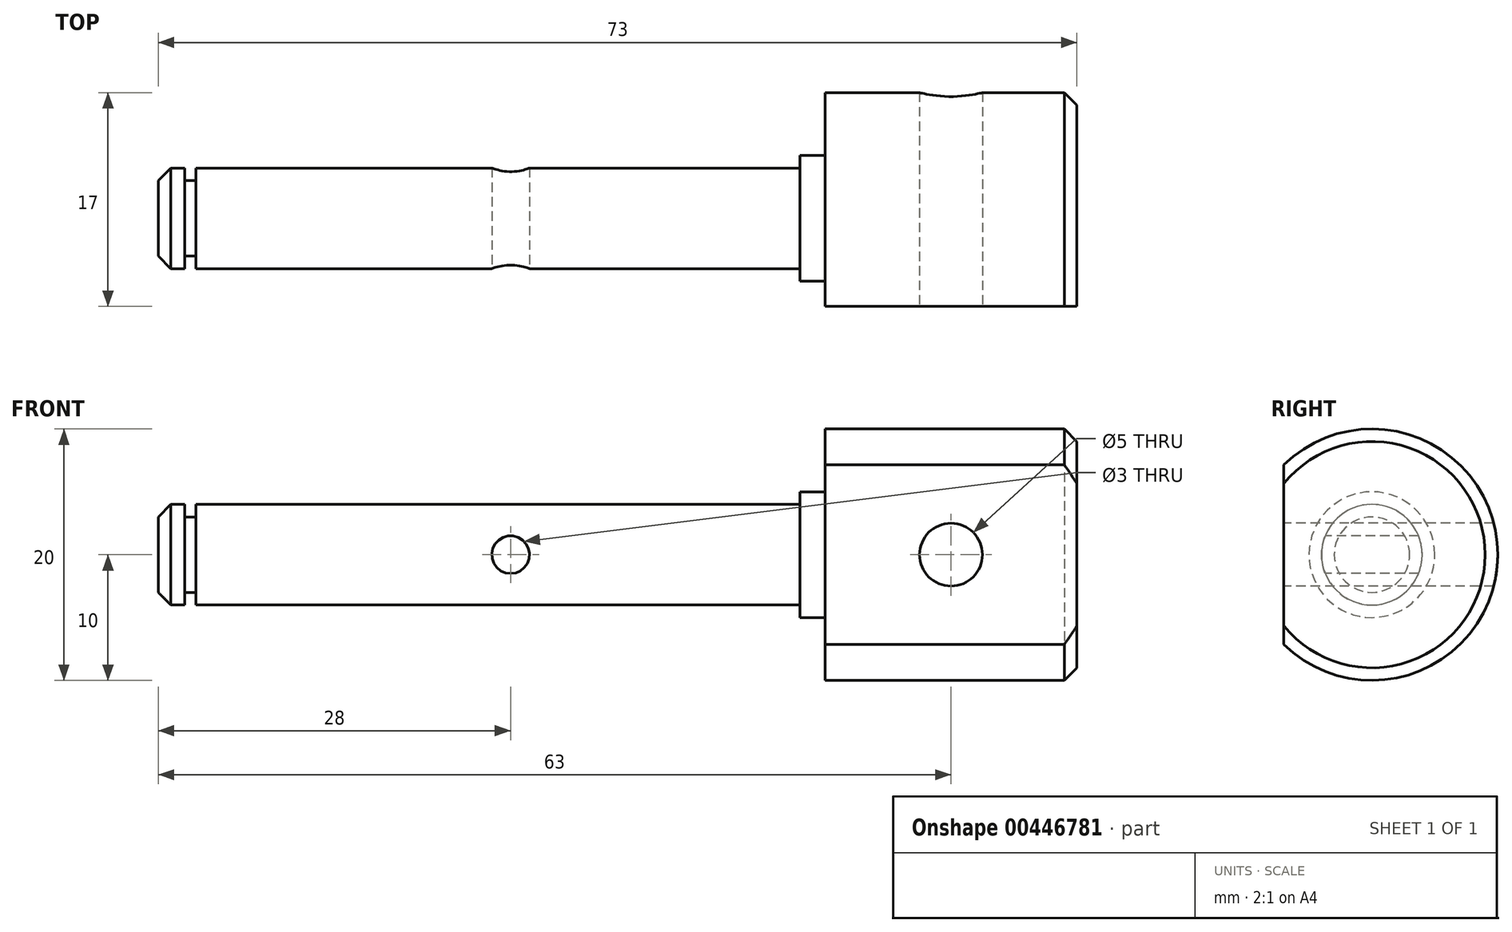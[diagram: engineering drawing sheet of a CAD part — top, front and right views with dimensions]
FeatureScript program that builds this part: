
annotation { "Feature Type Name" : "Feature", "Feature Type Description" : "" }
export const myFeature = defineFeature(function(context is Context, id is Id, definition is map)
    precondition{}
    {
        {
            var Q0;
            Q0=qCreatedBy(makeId("Front.planeOp"),FACE);
            var sketch = newSketch(context, id + "F0", { "sketchPlane" : qUnion([Q0])});
            skLineSegment(sketch, "E0", {"start": v(-56.66, 0) * mm, "end": v(24.86, 0) * mm, "construction": true});
            skLineSegment(sketch, "E1", {"start": v(0, 0) * mm, "end": v(20, 0) * mm});
            skLineSegment(sketch, "E2", {"start": v(20, 0) * mm, "end": v(20, 10) * mm});
            skLineSegment(sketch, "E3", {"start": v(20, 10) * mm, "end": v(0, 10) * mm});
            skLineSegment(sketch, "E4", {"start": v(0, 10) * mm, "end": v(0, 5) * mm});
            skLineSegment(sketch, "E5", {"start": v(0, 5) * mm, "end": v(-2, 5) * mm});
            skLineSegment(sketch, "E6", {"start": v(-2, 5) * mm, "end": v(-2, 4) * mm});
            skLineSegment(sketch, "E7", {"start": v(-2, 4) * mm, "end": v(-50, 4) * mm});
            skLineSegment(sketch, "E8", {"start": v(-50, 4) * mm, "end": v(-50, 3) * mm});
            skLineSegment(sketch, "E9", {"start": v(-50, 3) * mm, "end": v(-50.9, 3) * mm});
            skLineSegment(sketch, "E10", {"start": v(-50.9, 3) * mm, "end": v(-50.9, 4) * mm});
            skLineSegment(sketch, "E11", {"start": v(-50.9, 4) * mm, "end": v(-53, 4) * mm});
            skLineSegment(sketch, "E12", {"start": v(-53, 4) * mm, "end": v(-53, 0) * mm});
            skLineSegment(sketch, "E13", {"start": v(-53, 0) * mm, "end": v(0, 0) * mm});
            skSolve(sketch);
        }
        {
            var Q0;
            Q0 = qSketchRegion(id + "F0", true);
            var Q1;
            Q1=sQuery(id+"F0.wireOp",EDGE,"E0");
            revolve(context, id + "F1", {"entities" : qUnion([Q0]), "axis" : qUnion([Q1]), "revolveType" : RevolveType.FULL});
        }
        {
            var Q0;
            Q0=makeQuery(id+"F1.opRevolve","SWEPT_EDGE",EDGE,{"disambiguationData":[OSD([sQuery(id+"F0.wireOp",EDGE,"E11"),sQuery(id+"F0.wireOp",EDGE,"E12")])]});
            var Q1;
            Q1=makeQuery(id+"F1.opRevolve","SWEPT_EDGE",EDGE,{"disambiguationData":[OSD([sQuery(id+"F0.wireOp",EDGE,"E2"),sQuery(id+"F0.wireOp",EDGE,"E3")])]});
            chamfer(context, id + "F2", {"entities" : qUnion([Q0, Q1]), "width" : 1 * mm, "tangentPropagation" : true});
        }
        {
            var Q0;
            Q0=makeQuery(id+"F1.opRevolve","SWEPT_FACE",FACE,{"disambiguationData":[OSD([sQuery(id+"F0.wireOp",EDGE,"E2")])]});
            var sketch = newSketch(context, id + "F3", { "sketchPlane" : qUnion([Q0])});
            skArc(sketch, "E14.0", {"start": v(-7, 7.14) * mm, "mid": v(-10, 0) * mm, "end": v(-7, -7.14) * mm});
            skLineSegment(sketch, "E15", {"start": v(-7, 7.14) * mm, "end": v(-7, -7.14) * mm});
            skSolve(sketch);
        }
        {
            var Q0;
            Q0 = qSketchRegion(id + "F3", true);
            extrude(context, id + "F4", {"entities" : qUnion([Q0]), "operationType" : NewBodyOperationType.REMOVE, "endBound" : BoundingType.UP_TO_NEXT, "oppositeDirection" : true, "depth" : 25 * mm});
        }
        {
            var Q0;
            Q0=makeQuery(id+"F4.boolean.opBoolean","COPY",FACE,{"derivedFrom":makeQuery(id+"F4.opExtrude","SWEPT_FACE",FACE,{"disambiguationData":[OSD([sQuery(id+"F3.wireOp",EDGE,"E15")])]})});
            var sketch = newSketch(context, id + "F5", { "sketchPlane" : qUnion([Q0])});
            skCircle(sketch, "E16", {"center": v(10, 0) * mm, "radius": 2.5 * mm});
            skCircle(sketch, "E17", {"center": v(-25, 0) * mm, "radius": 1.5 * mm});
            skSolve(sketch);
        }
        {
            var Q0;
            Q0 = qSketchRegion(id + "F5", true);
            extrude(context, id + "F6", {"entities" : qUnion([Q0]), "operationType" : NewBodyOperationType.REMOVE, "endBound" : BoundingType.THROUGH_ALL, "oppositeDirection" : true, "depth" : 25 * mm});
        }
    });
